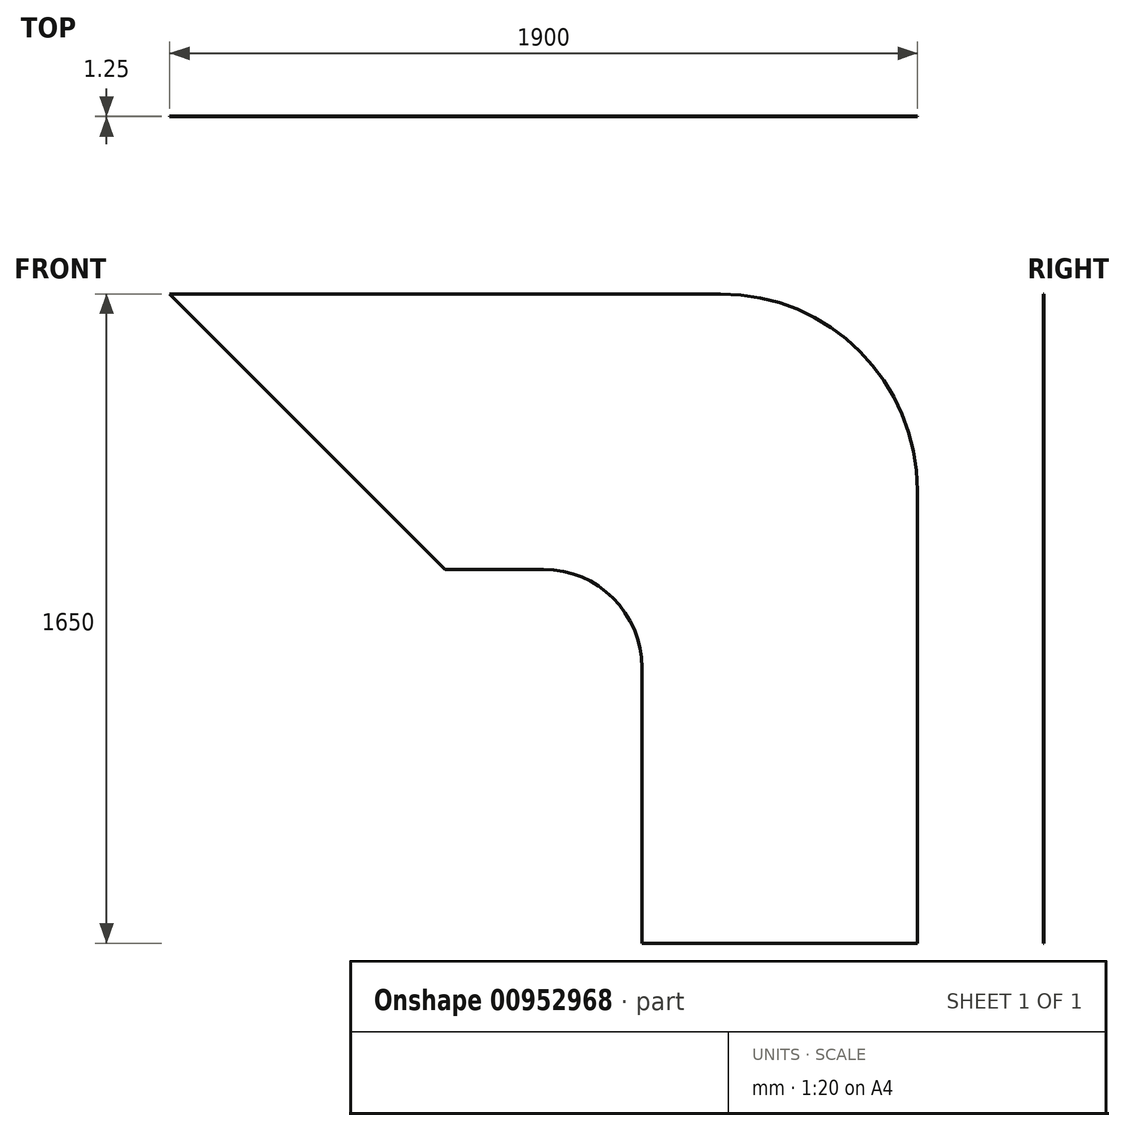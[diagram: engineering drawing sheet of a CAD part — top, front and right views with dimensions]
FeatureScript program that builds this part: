
annotation { "Feature Type Name" : "Feature", "Feature Type Description" : "" }
export const myFeature = defineFeature(function(context is Context, id is Id, definition is map)
    precondition{}
    {
        {
            var Q0;
            Q0=qCreatedBy(makeId("Front.planeOp"),FACE);
            var sketch = newSketch(context, id + "F0", { "sketchPlane" : qUnion([Q0])});
            skLineSegment(sketch, "E0", {"start": v(0, 0) * mm, "end": v(-700, 0) * mm});
            skLineSegment(sketch, "E1", {"start": v(-700, 0) * mm, "end": v(-700, 700) * mm});
            skLineSegment(sketch, "E2", {"start": v(-700, 700) * mm, "end": v(-950, 700) * mm});
            skCircle(sketch, "E3", {"center": v(-700, 700) * mm, "radius": 250 * mm});
            skLineSegment(sketch, "E4", {"start": v(-450, 700) * mm, "end": v(-450, 0) * mm});
            skLineSegment(sketch, "E5", {"start": v(-950, 700) * mm, "end": v(-950, 1650) * mm});
            skLineSegment(sketch, "E6", {"start": v(-950, 950) * mm, "end": v(-700, 950) * mm});
            skLineSegment(sketch, "E7", {"start": v(-450, 0) * mm, "end": v(250, 0) * mm});
            skLineSegment(sketch, "E8", {"start": v(250, 0) * mm, "end": v(250, 1150) * mm});
            skLineSegment(sketch, "E9", {"start": v(-950, 1650) * mm, "end": v(-250, 1650) * mm});
            skPoint(sketch, "E10.visualSharp", {"position": v(250, 1650) * mm});
            skArc(sketch, "E10.filletArc", {"start": v(250, 1150) * mm, "mid": v(103.55, 1503.55) * mm, "end": v(-250, 1650) * mm});
            skLineSegment(sketch, "E11", {"start": v(-950, 950) * mm, "end": v(-1650, 1650) * mm});
            skLineSegment(sketch, "E12", {"start": v(-950, 1650) * mm, "end": v(-1650, 1650) * mm});
            skSolve(sketch);
        }
        {
            var Q0;
            {var subQ3=sQuery(id+"F0.wireOp",EDGE,"E4");Q0=makeQuery(id+"F0.imprint","IMPRINT",FACE,{"disambiguationData":[TD([[makeQuery(id+"F0.imprint","IMPRINT",EDGE,{"derivedFrom":subQ3}),1.0]])]});}
            var Q1;
            {var subQ2=sQuery(id+"F0.wireOp",EDGE,"E11");Q1=makeQuery(id+"F0.imprint","IMPRINT",FACE,{"disambiguationData":[TD([[makeQuery(id+"F0.imprint","IMPRINT",EDGE,{"derivedFrom":subQ2}),-1.0]])]});}
            extrude(context, id + "F1", {"entities" : qUnion([Q0, Q1]), "depth" : 1.25 * mm, "offsetDistance" : 25 * mm});
        }
    });
